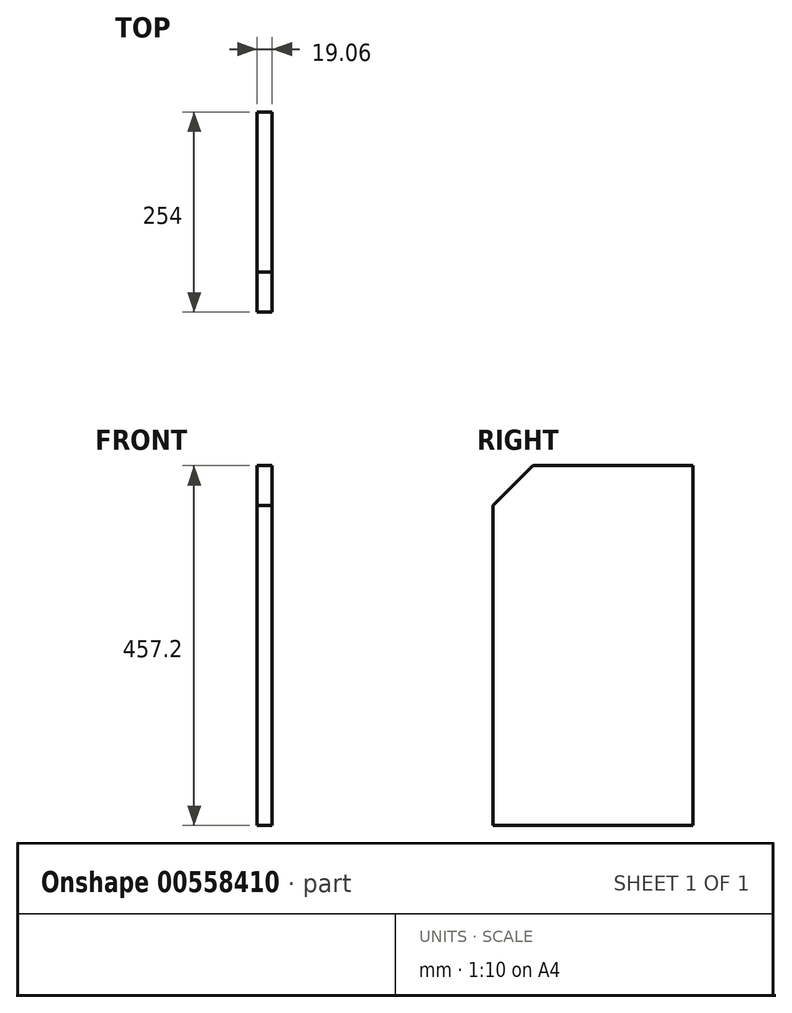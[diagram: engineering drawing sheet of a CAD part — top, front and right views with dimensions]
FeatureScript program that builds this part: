
annotation { "Feature Type Name" : "Feature", "Feature Type Description" : "" }
export const myFeature = defineFeature(function(context is Context, id is Id, definition is map)
    precondition{}
    {
        {
            var Q0;
            Q0=qCreatedBy(makeId("Right.planeOp"),FACE);
            var sketch = newSketch(context, id + "F0", { "sketchPlane" : qUnion([Q0])});
            skLineSegment(sketch, "E0.bottom", {"start": v(127, 228.6) * mm, "end": v(-127, 228.6) * mm});
            skLineSegment(sketch, "E0.top", {"start": v(127, -228.6) * mm, "end": v(-127, -228.6) * mm});
            skLineSegment(sketch, "E0.left", {"start": v(127, 228.6) * mm, "end": v(127, -228.6) * mm});
            skLineSegment(sketch, "E0.right", {"start": v(-127, 228.6) * mm, "end": v(-127, -228.6) * mm});
            skPoint(sketch, "E0.middle", {"position": v(0, 0) * mm});
            skSolve(sketch);
        }
        {
            var Q0;
            Q0=makeQuery(id+"F0.imprint","IMPRINT",FACE,{"disambiguationData":[TD([[makeQuery(id+"F0.imprint","IMPRINT",EDGE,{"derivedFrom":sQuery(id+"F0.wireOp",EDGE,"E0.bottom")}),1.0]])]});
            extrude(context, id + "F1", {"entities" : qUnion([Q0]), "endBound" : BoundingType.SYMMETRIC, "depth" : 19.05 * mm, "offsetDistance" : 25.4 * mm});
        }
        {
            var Q0;
            Q0=makeQuery(id+"F1.opExtrude","SWEPT_EDGE",EDGE,{"disambiguationData":[OSD([sQuery(id+"F0.wireOp",EDGE,"E0.bottom"),sQuery(id+"F0.wireOp",EDGE,"E0.right")])]});
            chamfer(context, id + "F2", {"entities" : qUnion([Q0]), "width" : 50.8 * mm, "tangentPropagation" : true});
        }
    });
